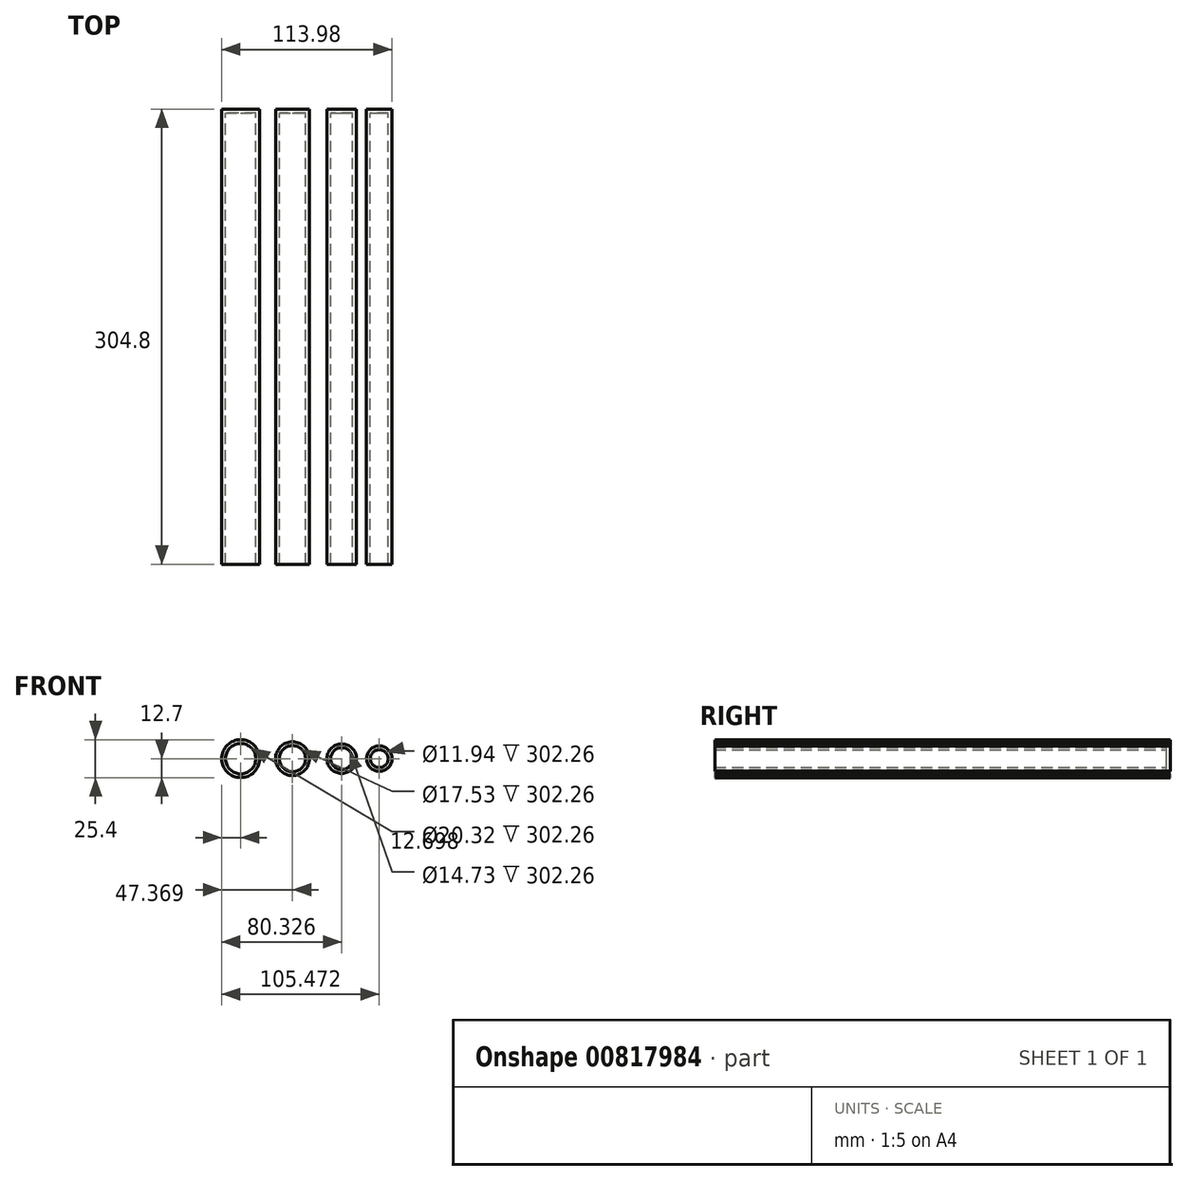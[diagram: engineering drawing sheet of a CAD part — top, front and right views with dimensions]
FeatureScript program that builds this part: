
annotation { "Feature Type Name" : "Feature", "Feature Type Description" : "" }
export const myFeature = defineFeature(function(context is Context, id is Id, definition is map)
    precondition{}
    {
        {
            var Q0;
            Q0=qCreatedBy(makeId("Front.planeOp"),FACE);
            var sketch = newSketch(context, id + "F0", { "sketchPlane" : qUnion([Q0])});
            skCircle(sketch, "E0", {"center": v(-55.91, 0) * mm, "radius": 12.7 * mm});
            skCircle(sketch, "E1", {"center": v(-21.24, 0) * mm, "radius": 11.3 * mm});
            skCircle(sketch, "E2", {"center": v(11.72, 0) * mm, "radius": 9.9 * mm});
            skCircle(sketch, "E3", {"center": v(36.86, 0) * mm, "radius": 8.5 * mm});
            skCircle(sketch, "E4.0", {"center": v(-55.91, 0) * mm, "radius": 10.16 * mm});
            skCircle(sketch, "E5.0", {"center": v(-21.24, 0) * mm, "radius": 8.76 * mm});
            skCircle(sketch, "E6.0", {"center": v(11.72, 0) * mm, "radius": 7.37 * mm});
            skCircle(sketch, "E7.0", {"center": v(36.86, 0) * mm, "radius": 5.97 * mm});
            skSolve(sketch);
        }
        {
            var Q0;
            Q0 = qSketchRegion(id + "F0", true);
            extrude(context, id + "F1", {"entities" : qUnion([Q0]), "depth" : 304.8 * mm, "offsetDistance" : 25.4 * mm});
        }
        {
            var Q0;
            Q0=makeQuery(id+"F0.imprint","IMPRINT",FACE,{"disambiguationData":[TD([[makeQuery(id+"F0.imprint","IMPRINT",EDGE,{"derivedFrom":sQuery(id+"F0.wireOp",EDGE,"E4.0")}),1.0]])]});
            var Q1;
            Q1=makeQuery(id+"F0.imprint","IMPRINT",FACE,{"disambiguationData":[TD([[makeQuery(id+"F0.imprint","IMPRINT",EDGE,{"derivedFrom":sQuery(id+"F0.wireOp",EDGE,"E5.0")}),1.0]])]});
            var Q2;
            Q2=makeQuery(id+"F0.imprint","IMPRINT",FACE,{"disambiguationData":[TD([[makeQuery(id+"F0.imprint","IMPRINT",EDGE,{"derivedFrom":sQuery(id+"F0.wireOp",EDGE,"E6.0")}),1.0]])]});
            var Q3;
            Q3=makeQuery(id+"F0.imprint","IMPRINT",FACE,{"disambiguationData":[TD([[makeQuery(id+"F0.imprint","IMPRINT",EDGE,{"derivedFrom":sQuery(id+"F0.wireOp",EDGE,"E7.0")}),1.0]])]});
            extrude(context, id + "F2", {"entities" : qUnion([Q0, Q1, Q2, Q3]), "operationType" : NewBodyOperationType.ADD, "depth" : 2.54 * mm, "offsetDistance" : 25.4 * mm});
        }
    });
